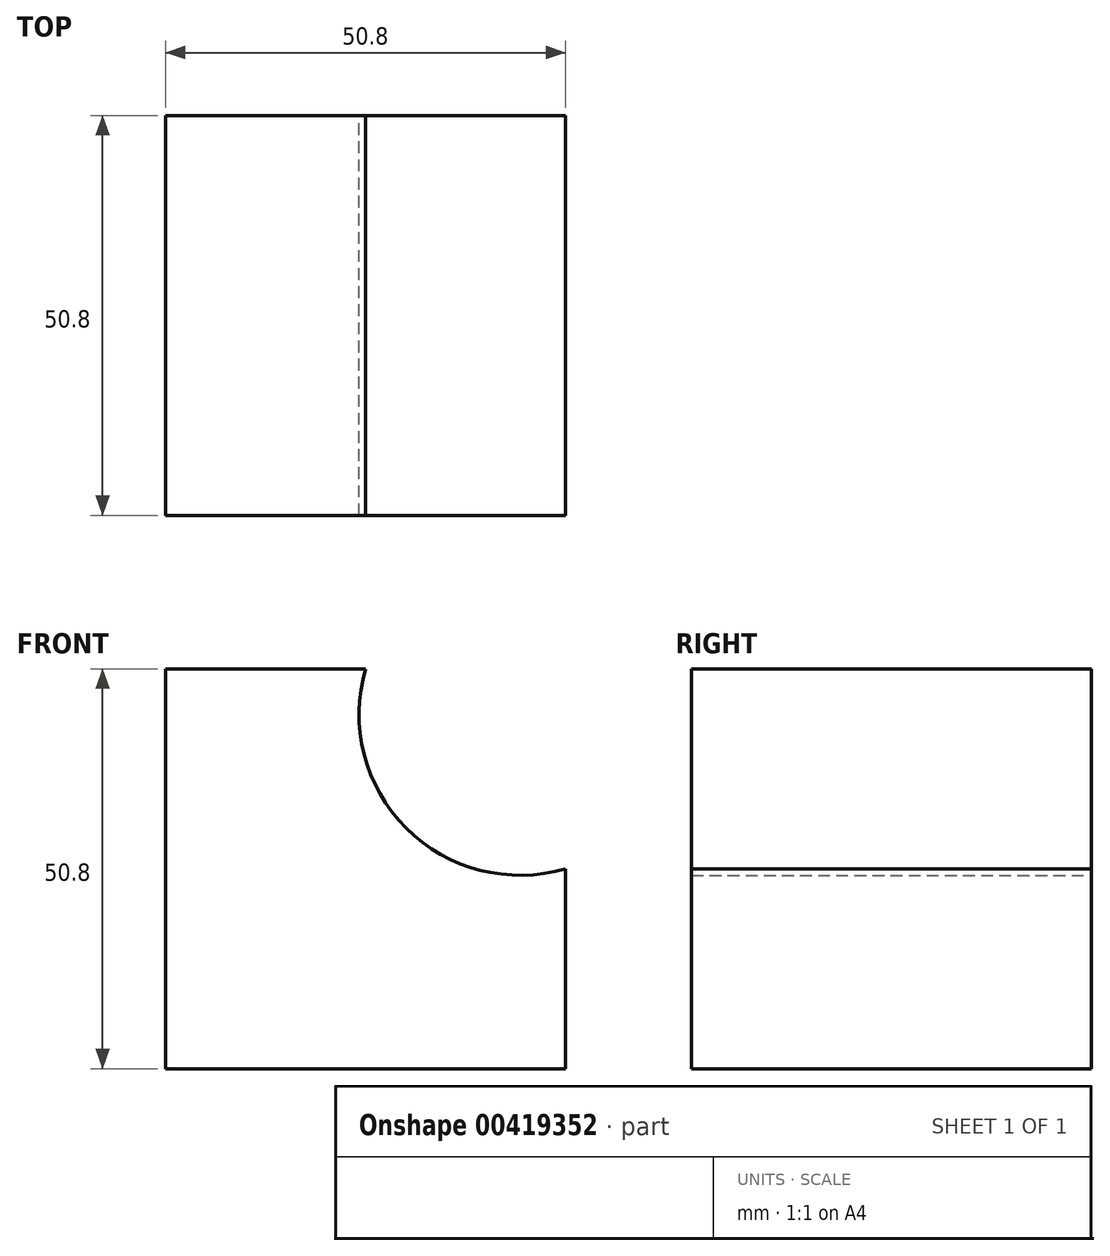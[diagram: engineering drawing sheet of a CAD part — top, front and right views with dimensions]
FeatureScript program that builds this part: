
annotation { "Feature Type Name" : "Feature", "Feature Type Description" : "" }
export const myFeature = defineFeature(function(context is Context, id is Id, definition is map)
    precondition{}
    {
        {
            var Q0;
            Q0=qCreatedBy(makeId("Front.planeOp"),FACE);
            var sketch = newSketch(context, id + "F0", { "sketchPlane" : qUnion([Q0])});
            skLineSegment(sketch, "E0", {"start": v(-4.39, 31.7) * mm, "end": v(-29.79, 31.7) * mm});
            skLineSegment(sketch, "E1", {"start": v(-29.79, 31.7) * mm, "end": v(-29.79, -19.1) * mm});
            skLineSegment(sketch, "E2", {"start": v(-29.79, -19.1) * mm, "end": v(21.01, -19.1) * mm});
            skLineSegment(sketch, "E3", {"start": v(21.01, -19.1) * mm, "end": v(21.01, 6.3) * mm});
            skArc(sketch, "E4", {"start": v(-4.39, 31.7) * mm, "mid": v(0.76, 11.46) * mm, "end": v(21.01, 6.3) * mm});
            skSolve(sketch);
        }
        {
            var Q0;
            Q0 = qSketchRegion(id + "F0", true);
            extrude(context, id + "F1", {"entities" : qUnion([Q0]), "depth" : 50.8 * mm});
        }
    });
